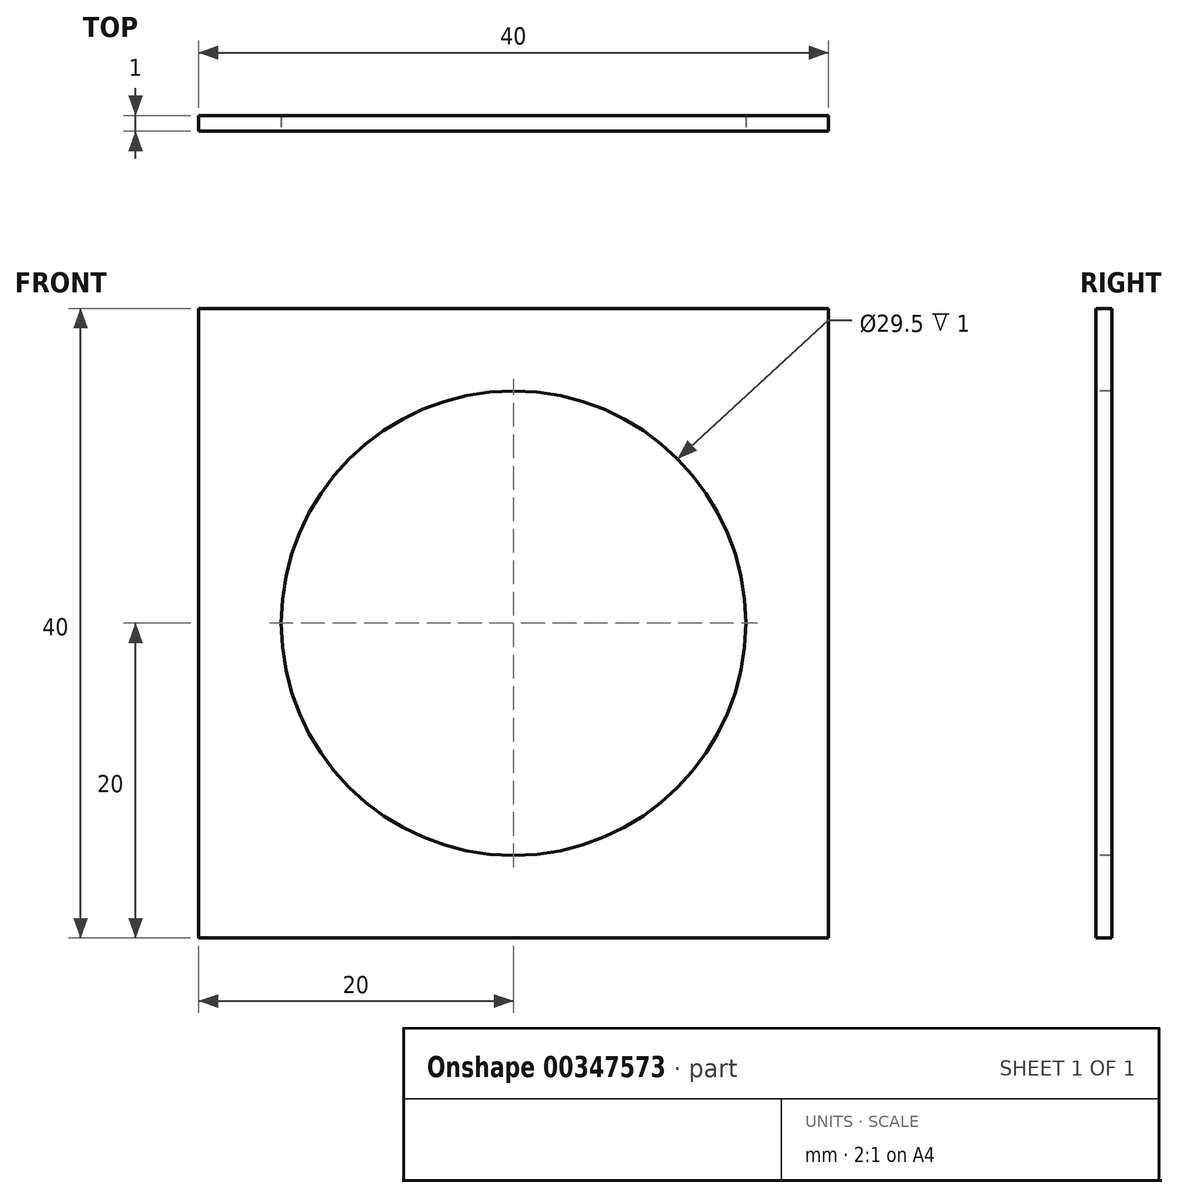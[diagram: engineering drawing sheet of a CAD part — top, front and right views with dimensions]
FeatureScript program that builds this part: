
annotation { "Feature Type Name" : "Feature", "Feature Type Description" : "" }
export const myFeature = defineFeature(function(context is Context, id is Id, definition is map)
    precondition{}
    {
        {
            var Q0;
            Q0=qCreatedBy(makeId("Front.planeOp"),FACE);
            var sketch = newSketch(context, id + "F0", { "sketchPlane" : qUnion([Q0])});
            skLineSegment(sketch, "E0.bottom", {"start": v(20, 20) * mm, "end": v(-20, 20) * mm});
            skLineSegment(sketch, "E0.top", {"start": v(20, -20) * mm, "end": v(-20, -20) * mm});
            skLineSegment(sketch, "E0.left", {"start": v(20, 20) * mm, "end": v(20, -20) * mm});
            skLineSegment(sketch, "E0.right", {"start": v(-20, 20) * mm, "end": v(-20, -20) * mm});
            skPoint(sketch, "E0.middle", {"position": v(0, 0) * mm});
            skSolve(sketch);
        }
        {
            var Q0;
            Q0 = qSketchRegion(id + "F0", true);
            extrude(context, id + "F1", {"entities" : qUnion([Q0]), "depth" : 1 * mm});
        }
        {
            var Q0;
            Q0=makeQuery(id+"F1.opExtrude","CAP_FACE",FACE,{"disambiguationData":[OSD([sQuery(id+"F0.wireOp",EDGE,"E0.bottom"),sQuery(id+"F0.wireOp",EDGE,"E0.top"),sQuery(id+"F0.wireOp",EDGE,"E0.left"),sQuery(id+"F0.wireOp",EDGE,"E0.right")])],"isStart":false});
            var sketch = newSketch(context, id + "F2", { "sketchPlane" : qUnion([Q0])});
            skCircle(sketch, "E1", {"center": v(0, 0) * mm, "radius": 14.75 * mm});
            skSolve(sketch);
        }
        {
            var Q0;
            Q0=makeQuery(id+"F2.imprint","IMPRINT",FACE,{"disambiguationData":[TD([[makeQuery(id+"F2.imprint","IMPRINT",EDGE,{"derivedFrom":sQuery(id+"F2.wireOp",EDGE,"E1")}),1.0]])]});
            extrude(context, id + "F3", {"entities" : qUnion([Q0]), "operationType" : NewBodyOperationType.REMOVE, "oppositeDirection" : true, "depth" : 1 * mm});
        }
    });
